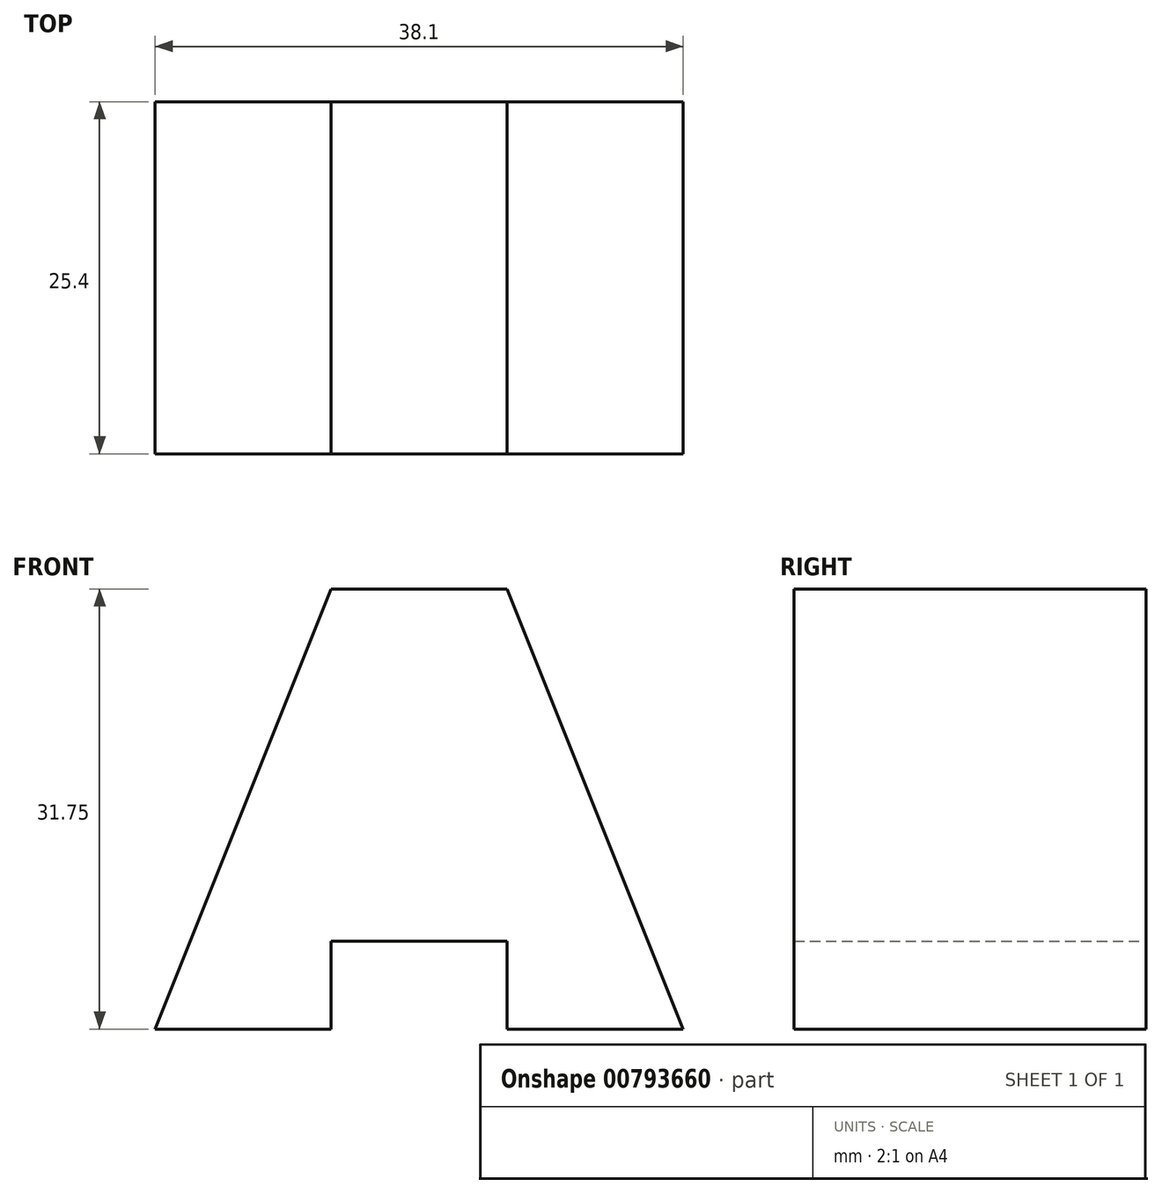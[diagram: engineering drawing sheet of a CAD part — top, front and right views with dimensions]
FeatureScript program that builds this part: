
annotation { "Feature Type Name" : "Feature", "Feature Type Description" : "" }
export const myFeature = defineFeature(function(context is Context, id is Id, definition is map)
    precondition{}
    {
        {
            var Q0;
            Q0=qCreatedBy(makeId("Front.planeOp"),FACE);
            var sketch = newSketch(context, id + "F0", { "sketchPlane" : qUnion([Q0])});
            skLineSegment(sketch, "E0", {"start": v(0, 0) * mm, "end": v(12.7, 0) * mm});
            skLineSegment(sketch, "E1", {"start": v(12.7, 0) * mm, "end": v(12.7, 6.35) * mm});
            skLineSegment(sketch, "E2", {"start": v(12.7, 6.35) * mm, "end": v(25.4, 6.35) * mm});
            skLineSegment(sketch, "E3", {"start": v(25.4, 6.35) * mm, "end": v(25.4, 0) * mm});
            skLineSegment(sketch, "E4", {"start": v(25.4, 0) * mm, "end": v(38.1, 0) * mm});
            skLineSegment(sketch, "E5", {"start": v(38.1, 0) * mm, "end": v(25.4, 31.75) * mm});
            skLineSegment(sketch, "E6", {"start": v(25.4, 31.75) * mm, "end": v(12.7, 31.75) * mm});
            skLineSegment(sketch, "E7", {"start": v(12.7, 31.75) * mm, "end": v(0, 0) * mm});
            skSolve(sketch);
        }
        {
            var Q0;
            Q0=makeQuery(id+"F0.imprint","IMPRINT",FACE,{"disambiguationData":[TD([[makeQuery(id+"F0.imprint","IMPRINT",EDGE,{"derivedFrom":sQuery(id+"F0.wireOp",EDGE,"E0")}),1.0]])]});
            extrude(context, id + "F1", {"entities" : qUnion([Q0]), "depth" : 25.4 * mm, "offsetDistance" : 25.4 * mm});
        }
    });
